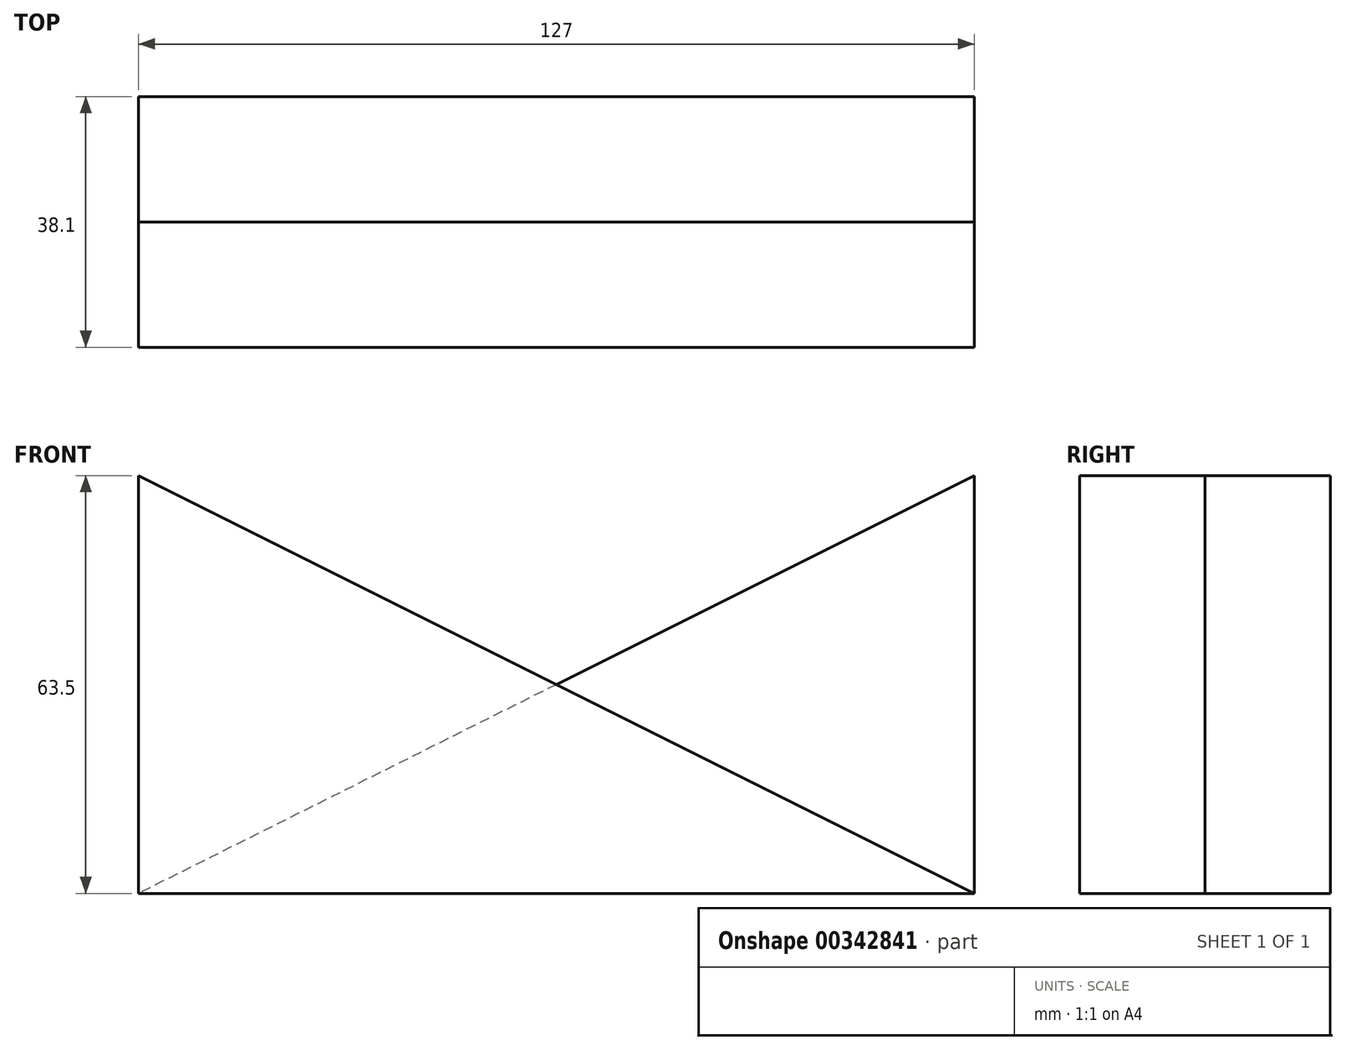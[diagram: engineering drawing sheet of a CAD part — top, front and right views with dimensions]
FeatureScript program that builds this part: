
annotation { "Feature Type Name" : "Feature", "Feature Type Description" : "" }
export const myFeature = defineFeature(function(context is Context, id is Id, definition is map)
    precondition{}
    {
        {
            var Q0;
            Q0=qCreatedBy(makeId("Front.planeOp"),FACE);
            var sketch = newSketch(context, id + "F0", { "sketchPlane" : qUnion([Q0])});
            skLineSegment(sketch, "E0.top", {"start": v(63.5, -31.75) * mm, "end": v(-63.5, -31.75) * mm});
            skLineSegment(sketch, "E0.left", {"start": v(63.5, 31.75) * mm, "end": v(63.5, -31.75) * mm});
            skLineSegment(sketch, "E0.right", {"start": v(-63.5, 31.75) * mm, "end": v(-63.5, -31.75) * mm});
            skPoint(sketch, "E0.middle", {"position": v(0, 0) * mm});
            skLineSegment(sketch, "E1", {"start": v(-63.5, 31.75) * mm, "end": v(63.5, -31.75) * mm});
            skLineSegment(sketch, "E2", {"start": v(63.5, 31.75) * mm, "end": v(-63.5, -31.75) * mm});
            skSolve(sketch);
        }
        {
            var Q0;
            {var subQ0=sQuery(id+"F0.wireOp",EDGE,"E0.right");Q0=makeQuery(id+"F0.imprint","IMPRINT",FACE,{"disambiguationData":[TD([[makeQuery(id+"F0.imprint","IMPRINT",EDGE,{"derivedFrom":subQ0}),1.0]])]});}
            var Q1;
            {var subQ0=sQuery(id+"F0.wireOp",EDGE,"E0.top");Q1=makeQuery(id+"F0.imprint","IMPRINT",FACE,{"disambiguationData":[TD([[makeQuery(id+"F0.imprint","IMPRINT",EDGE,{"derivedFrom":subQ0}),-1.0]])]});}
            extrude(context, id + "F1", {"entities" : qUnion([Q0, Q1]), "depth" : 19.05 * mm});
        }
        {
            var Q0;
            {var subQ0=sQuery(id+"F0.wireOp",EDGE,"E0.left");Q0=makeQuery(id+"F0.imprint","IMPRINT",FACE,{"disambiguationData":[TD([[makeQuery(id+"F0.imprint","IMPRINT",EDGE,{"derivedFrom":subQ0}),-1.0]])]});}
            var Q1;
            {var subQ0=sQuery(id+"F0.wireOp",EDGE,"E0.top");Q1=makeQuery(id+"F0.imprint","IMPRINT",FACE,{"disambiguationData":[TD([[makeQuery(id+"F0.imprint","IMPRINT",EDGE,{"derivedFrom":subQ0}),-1.0]])]});}
            extrude(context, id + "F2", {"entities" : qUnion([Q0, Q1]), "operationType" : NewBodyOperationType.ADD, "oppositeDirection" : true, "depth" : 19.05 * mm});
        }
    });
